# Revit family: dbcee23b-5128-4a59-89fe-01d847426539
name_source: partatom
category: Specialty Equipment
units: mm (PartAtom-declared; Revit-internal decimal feet)

## family parameters
Cut with Voids When Loaded = No
Host = Face
Part Type = Normal
Room Calculation Point = No
Round Connector Dimension = Use Diameter
Shared = No

## types (1)
- DSM - .5 inches
    ABAA Compliance = Yes
    Assembly Code = C3020200
    Default Elevation = 0' - 0"
    Depth = 0' - 1 3/4"
    Description = Watertight trafficable expansion joint for decks, walkways, ramps and roadways
    Durometer Hardness of Silicone Coating (ASTM D2240) = Shore A: 15
    Manufacturer = EMSEAL Joint Systems Ltd
    Manufacturer URL = http://www.emseal.com
    Model = DSM
    Movement (of Nominal Material Size) = +50% / -50%
    Pick Resistance = No
    Product Documentataion URL = https://bit.ly
    Product Page URL = https://www.emseal.com
    Quad Bellow = No
    R Value Range (ASTM C518) = 1.8 per 1-inch (25mm) depth
    Rate of Air Leakage (ASTM E283) = Passed
    Seal Material = Silicone - Sikasil WS-295 Deck Gray
    Seal Material Note = DSM is coated on the top traffic side with standard Sikasil WS-295 water-resistant traffic-grade silicone
    Single Bellow = Yes
    Staining (ASTM C510) = None
    Temperature Range (ASTM C711) = 185°F (85°C) to -40°F (-40°C)
    Tensile Strength (ASTM D3574) = 18 psi min; 145 kPa
    Triple Bellow = No
    Type Image = DSM.PNG
    Width = 0' - 0 1/2"

## geometry (parser evidence)
native form markers: Sweep x2
no freeform markers — native parametric forms only
